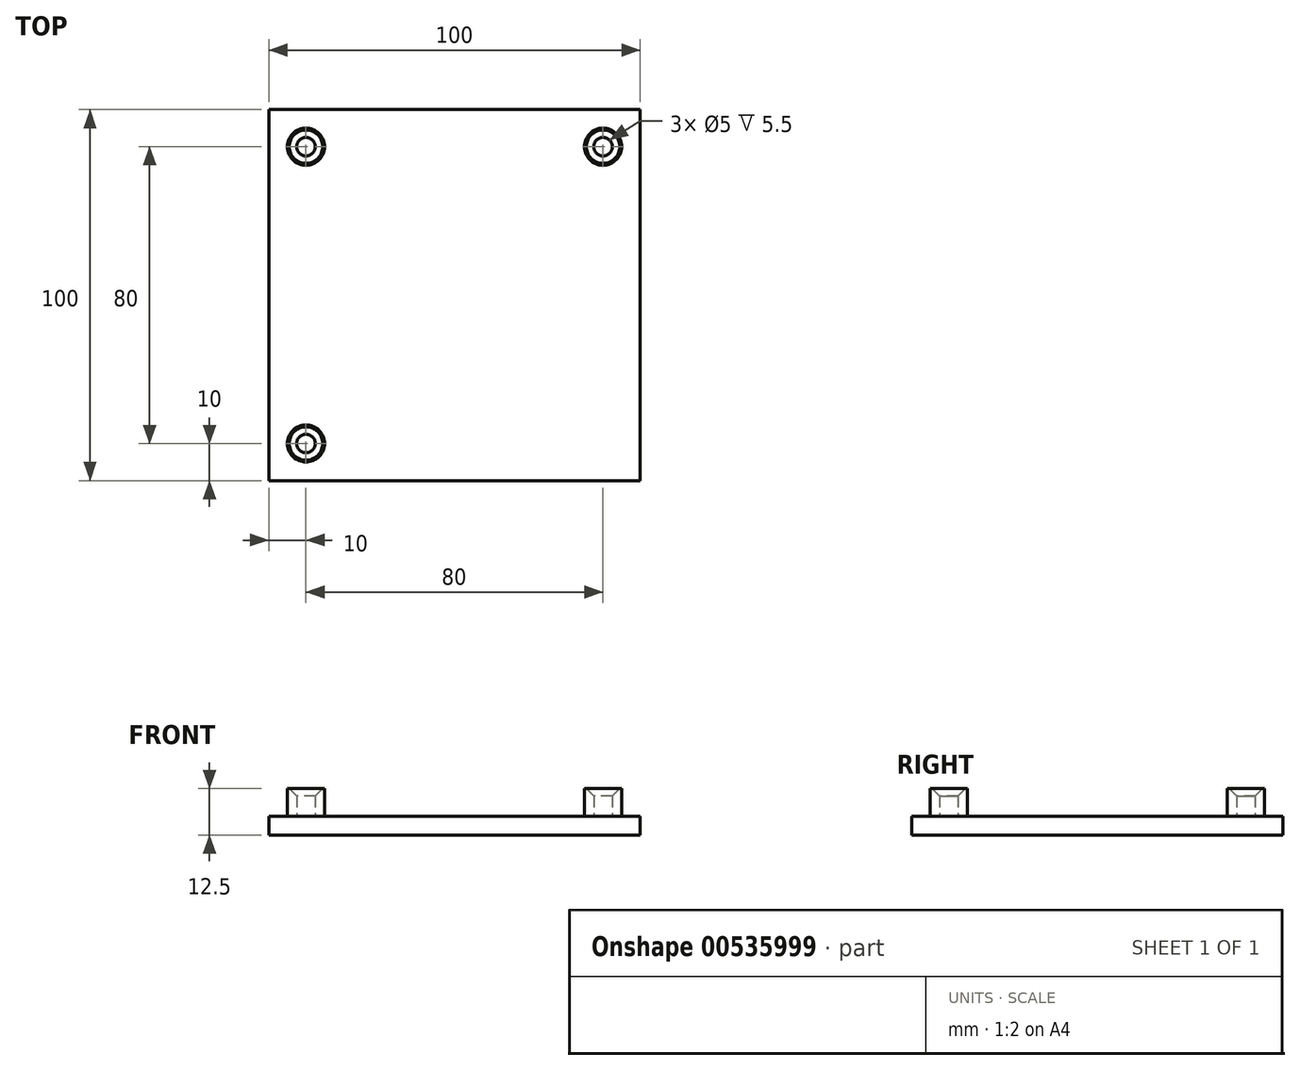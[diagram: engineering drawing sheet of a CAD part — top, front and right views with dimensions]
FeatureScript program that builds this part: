
annotation { "Feature Type Name" : "Feature", "Feature Type Description" : "" }
export const myFeature = defineFeature(function(context is Context, id is Id, definition is map)
    precondition{}
    {
        {
            var Q0;
            Q0=qCreatedBy(makeId("Top.planeOp"),FACE);
            var sketch = newSketch(context, id + "F0", { "sketchPlane" : qUnion([Q0])});
            skLineSegment(sketch, "E0.bottom", {"start": v(50, 50) * mm, "end": v(-50, 50) * mm});
            skLineSegment(sketch, "E0.top", {"start": v(50, -50) * mm, "end": v(-50, -50) * mm});
            skLineSegment(sketch, "E0.left", {"start": v(50, 50) * mm, "end": v(50, -50) * mm});
            skLineSegment(sketch, "E0.right", {"start": v(-50, 50) * mm, "end": v(-50, -50) * mm});
            skPoint(sketch, "E0.middle", {"position": v(0, 0) * mm});
            skSolve(sketch);
        }
        {
            var Q0;
            Q0 = qSketchRegion(id + "F0", true);
            extrude(context, id + "F1", {"entities" : qUnion([Q0]), "depth" : 5 * mm, "offsetDistance" : 25 * mm});
        }
        {
            var Q0;
            Q0=makeQuery(id+"F1.opExtrude","CAP_FACE",FACE,{"disambiguationData":[OSD([sQuery(id+"F0.wireOp",EDGE,"E0.bottom"),sQuery(id+"F0.wireOp",EDGE,"E0.top"),sQuery(id+"F0.wireOp",EDGE,"E0.left"),sQuery(id+"F0.wireOp",EDGE,"E0.right")])],"isStart":false});
            var sketch = newSketch(context, id + "F2", { "sketchPlane" : qUnion([Q0])});
            skCircle(sketch, "E1", {"center": v(-40, 40) * mm, "radius": 5 * mm});
            skCircle(sketch, "E2", {"center": v(-40, 40) * mm, "radius": 2.5 * mm});
            skCircle(sketch, "E3", {"center": v(-40, -40) * mm, "radius": 5 * mm});
            skCircle(sketch, "E4", {"center": v(-40, -40) * mm, "radius": 2.5 * mm});
            skCircle(sketch, "E5", {"center": v(40, 40) * mm, "radius": 5 * mm});
            skCircle(sketch, "E6", {"center": v(40, 40) * mm, "radius": 2.5 * mm});
            skSolve(sketch);
        }
        {
            var Q0;
            Q0 = qSketchRegion(id + "F2", true);
            extrude(context, id + "F3", {"entities" : qUnion([Q0]), "operationType" : NewBodyOperationType.ADD, "depth" : 5 * mm, "offsetDistance" : 25 * mm});
        }
        {
            var Q0;
            Q0=makeQuery(id+"F1.opExtrude","SWEPT_FACE",FACE,{"disambiguationData":[OSD([sQuery(id+"F0.wireOp",EDGE,"E0.bottom")])]});
            cPlane(context, id + "F4", {"entities" : qUnion([Q0]), "cplaneType" : CPlaneType.OFFSET, "offset" : 10 * mm, "oppositeDirection" : true, "width" : 150 * mm, "height" : 150 * mm});
        }
        {
            var Q0;
            Q0=qCreatedBy(id+"F4.planeOp",FACE);
            var sketch = newSketch(context, id + "F5", { "sketchPlane" : qUnion([Q0])});
            skCircle(sketch, "E7", {"center": v(40, 15) * mm, "radius": 5 * mm, "construction": true});
            skSolve(sketch);
        }
        {
            var Q0;
            Q0=makeQuery(id+"F3.opExtrude","CAP_FACE",FACE,{"disambiguationData":[OSD([sQuery(id+"F2.wireOp",EDGE,"E1"),sQuery(id+"F2.wireOp",EDGE,"E2")])],"isStart":false});
            var sketch = newSketch(context, id + "F6", { "sketchPlane" : qUnion([Q0])});
            skCircle(sketch, "E8.0", {"center": v(-40, -40) * mm, "radius": 2.5 * mm});
            skCircle(sketch, "E8.1", {"center": v(-40, -40) * mm, "radius": 5 * mm});
            skCircle(sketch, "E9.0", {"center": v(40, 40) * mm, "radius": 5 * mm});
            skCircle(sketch, "E9.1", {"center": v(40, 40) * mm, "radius": 2.5 * mm});
            skCircle(sketch, "E9.2", {"center": v(-40, 40) * mm, "radius": 2.5 * mm});
            skCircle(sketch, "E9.3", {"center": v(-40, 40) * mm, "radius": 5 * mm});
            skSolve(sketch);
        }
        {
            var Q0;
            Q0 = qSketchRegion(id + "F6", true);
            var Q1;
            Q1 = qSketchRegion(id + "F5", true);
            extrude(context, id + "F7", {"entities" : qUnion([Q0, Q1]), "operationType" : NewBodyOperationType.ADD, "depth" : 2.5 * mm, "offsetDistance" : 25 * mm});
        }
        {
            var Q0;
            Q0=makeQuery(id+"F7.opExtrude","CAP_EDGE",EDGE,{"disambiguationData":[OSD([sQuery(id+"F6.wireOp",EDGE,"E9.2")])],"isStart":false});
            var Q1;
            Q1=makeQuery(id+"F7.opExtrude","CAP_EDGE",EDGE,{"disambiguationData":[OSD([sQuery(id+"F6.wireOp",EDGE,"E8.0")])],"isStart":false});
            var Q2;
            Q2=makeQuery(id+"F7.opExtrude","CAP_EDGE",EDGE,{"disambiguationData":[OSD([sQuery(id+"F6.wireOp",EDGE,"E9.1")])],"isStart":false});
            chamfer(context, id + "F8", {"entities" : qUnion([Q0, Q1, Q2]), "width" : 2 * mm, "tangentPropagation" : true});
        }
    });
